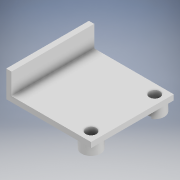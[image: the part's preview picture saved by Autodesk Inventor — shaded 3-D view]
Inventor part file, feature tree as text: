
AUTODESK INVENTOR PART (.ipt)
format: ipt  version: 2020 (Build 240168000, 168)  size: 171,008 bytes
history: native  units: mm
features: extrude x4, sketch x4, projected_geometry x2
ambient origin geometry x8: Origin, YZ Plane, XZ Plane, XY Plane, X Axis, Y Axis, Z Axis, Center Point
bodies: Solid1 (feature_tree)
feature tree (10):
  extrude  "Extrusion1"  Depth=2.0mm
  extrude  "Extrusion2"  Depth=1.8mm
  extrude  "Extrusion3"  Depth=1.8mm
  extrude  "Extrusion4"  Depth=1.8mm
  sketch  "Sketch1"  dims[d2=2.0mm d3=2.0mm]
  sketch  "Sketch2"  dims[d4=1.8mm d5=1.8mm]
  projected_geometry  "Projected Loop1"
  sketch  "Sketch3"  dims[d6=1.8mm d7=1.8mm]
  projected_geometry  "Projected Loop2"
  sketch  "Sketch4"  dims[d8=14.0mm d9=1.8mm d10=2.6mm d11=3.6mm d12=3.6mm d13=1.0mm d14=1.0mm d15=1.8mm d16=0.0mm d18=1.8mm d19=1.0mm d20=0.0mm d21=12.4mm d22=0.0mm d23=1.0mm d24=4.0mm d25=0.0mm d17=0.5mm]
